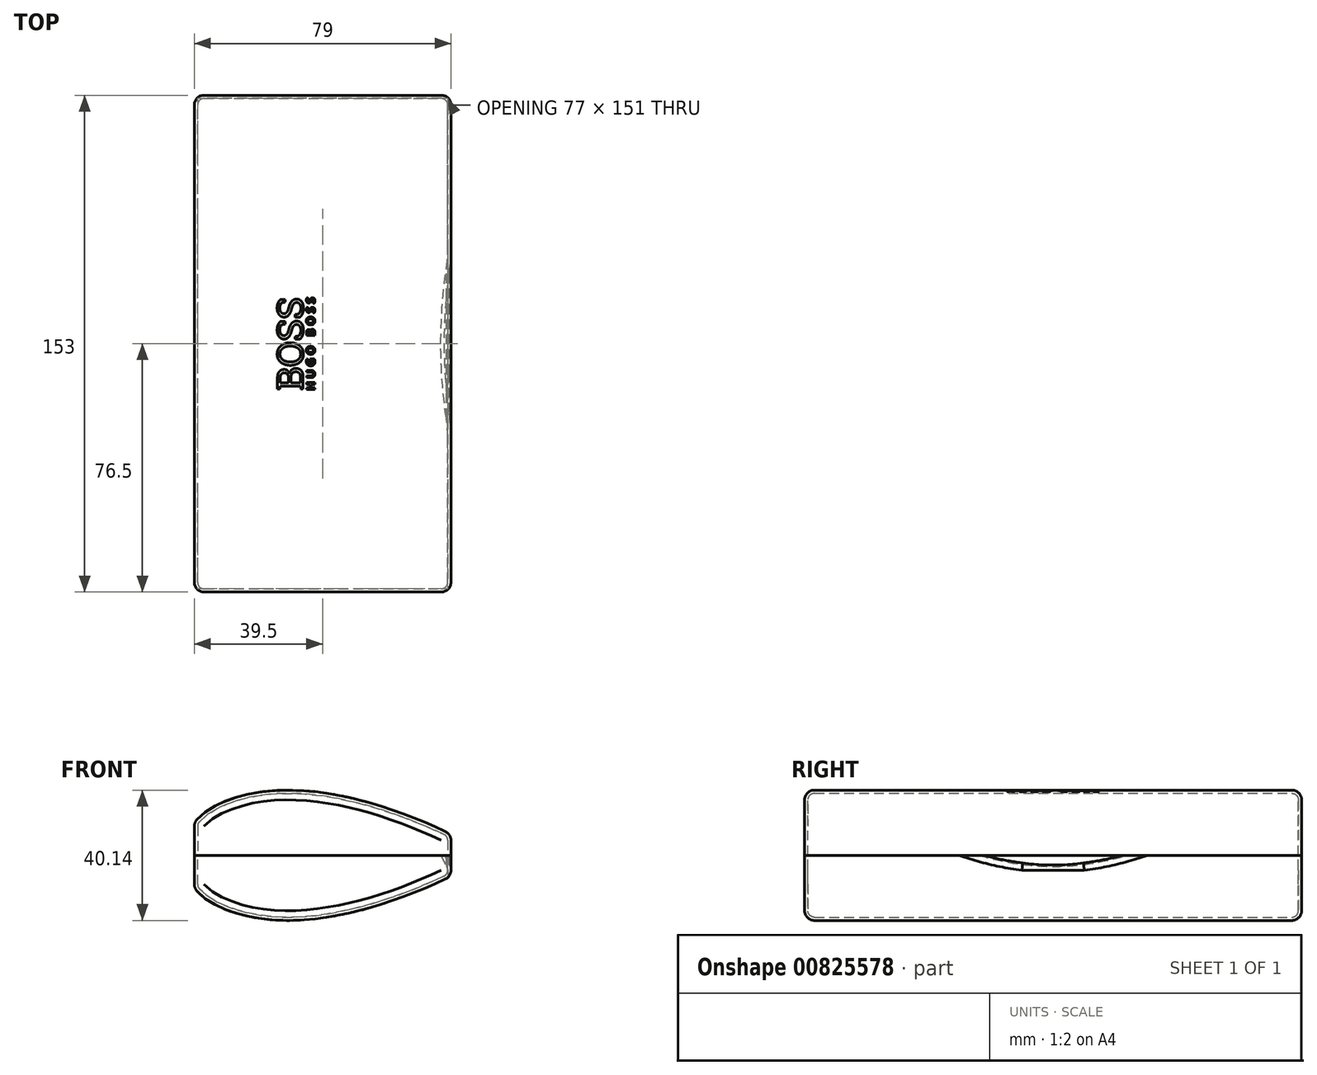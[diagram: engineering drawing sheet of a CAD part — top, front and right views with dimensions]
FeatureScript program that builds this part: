
annotation { "Feature Type Name" : "Feature", "Feature Type Description" : "" }
export const myFeature = defineFeature(function(context is Context, id is Id, definition is map)
    precondition{}
    {
        {
            var Q0;
            Q0=qCreatedBy(makeId("Front.planeOp"),FACE);
            var sketch = newSketch(context, id + "F0", { "sketchPlane" : qUnion([Q0])});
            skLineSegment(sketch, "E0", {"start": v(-39.5, 0) * mm, "end": v(39.5, 0) * mm});
            skLineSegment(sketch, "E1", {"start": v(39.5, 6.5) * mm, "end": v(39.5, -6.5) * mm});
            skLineSegment(sketch, "E2", {"start": v(-39.5, 10) * mm, "end": v(-39.5, -10) * mm});
            skPoint(sketch, "E3", {"position": v(-14.5, 20) * mm});
            skPoint(sketch, "E4", {"position": v(-39.5, 0) * mm});
            skFitSpline(sketch, "E5", {"points": [v(-39.5, 10) * mm, v(-13.74, 20) * mm, v(39.5, 6.5) * mm], "startDerivative": vector(26.63, 38.18) * mm, "endDerivative": vector(85.64, -41.52) * mm});
            skSolve(sketch);
        }
        {
            var Q0;
            {var subQ0=sQuery(id+"F0.wireOp",EDGE,"E0");Q0=makeQuery(id+"F0.imprint","IMPRINT",FACE,{"disambiguationData":[TD([[makeQuery(id+"F0.imprint","IMPRINT",EDGE,{"derivedFrom":subQ0}),1.0]])]});}
            extrude(context, id + "F1", {"entities" : qUnion([Q0]), "endBound" : BoundingType.SYMMETRIC, "depth" : 153 * mm, "offsetDistance" : 25 * mm});
        }
        {
            var Q0;
            Q0=makeQuery(id+"F1.opExtrude","SWEPT_BODY",BODY,{"disambiguationData":[OSD([sQuery(id+"F0.wireOp",EDGE,"E0"),sQuery(id+"F0.wireOp",EDGE,"E1"),sQuery(id+"F0.wireOp",EDGE,"E2"),sQuery(id+"F0.wireOp",EDGE,"E5")])]});
            var Q1;
            Q1=makeQuery(id+"F1.opExtrude","SWEPT_FACE",FACE,{"disambiguationData":[OSD([sQuery(id+"F0.wireOp",EDGE,"E0")])]});
            mirror(context, id + "F2", {"entities" : qUnion([Q0]), "mirrorPlane" : qUnion([Q1])});
        }
        {
            var Q0;
            Q0=makeQuery(id+"F2.opPattern","COPY",FACE,{"derivedFrom":makeQuery(id+"F1.opExtrude","SWEPT_FACE",FACE,{"disambiguationData":[OSD([sQuery(id+"F0.wireOp",EDGE,"E0")])]}),"instanceName":"1"});
            var sketch = newSketch(context, id + "F3", { "sketchPlane" : qUnion([Q0])});
            skLineSegment(sketch, "E6", {"start": v(0, 0) * mm, "end": v(39.5, 0) * mm, "construction": true});
            skLineSegment(sketch, "E7", {"start": v(39.5, 25) * mm, "end": v(39.5, -25) * mm});
            skLineSegment(sketch, "E8", {"start": v(39.5, 0) * mm, "end": v(37.5, 0) * mm, "construction": true});
            skArc(sketch, "E9", {"start": v(39.5, 25) * mm, "mid": v(37.5, 0) * mm, "end": v(39.5, -25) * mm});
            skSolve(sketch);
        }
        {
            var Q0;
            Q0=qCreatedBy(makeId("Front.planeOp"),FACE);
            var sketch = newSketch(context, id + "F4", { "sketchPlane" : qUnion([Q0])});
            skPoint(sketch, "E10", {"position": v(37.5, 0) * mm});
            skPoint(sketch, "E11", {"position": v(39.5, -4) * mm});
            skLineSegment(sketch, "E12", {"start": v(37.5, 0) * mm, "end": v(39.5, -4) * mm});
            skSolve(sketch);
        }
        {
            var Q0;
            Q0=makeQuery(id+"F3.imprint","IMPRINT",FACE,{"disambiguationData":[TD([[makeQuery(id+"F3.imprint","IMPRINT",EDGE,{"derivedFrom":sQuery(id+"F3.wireOp",EDGE,"E7")}),1.0]])]});
            var Q1;
            Q1=sQuery(id+"F4.wireOp",EDGE,"E12");
            sweep(context, id + "F5", {"operationType" : NewBodyOperationType.REMOVE, "profiles" : qUnion([Q0]), "path" : qUnion([Q1])});
        }
        {
            var Q0;
            Q0=makeQuery(id+"F1.opExtrude","SWEPT_FACE",FACE,{"disambiguationData":[OSD([sQuery(id+"F0.wireOp",EDGE,"E5")])]});
            var Q1;
            Q1=makeQuery(id+"F2.opPattern","COPY",FACE,{"derivedFrom":makeQuery(id+"F1.opExtrude","SWEPT_FACE",FACE,{"disambiguationData":[OSD([sQuery(id+"F0.wireOp",EDGE,"E5")])]}),"instanceName":"1"});
            var Q2;
            Q2=makeQuery(id+"F1.opExtrude","CAP_EDGE",EDGE,{"disambiguationData":[OSD([sQuery(id+"F0.wireOp",EDGE,"E1")])],"isStart":false});
            var Q3;
            Q3=makeQuery(id+"F2.opPattern","COPY",EDGE,{"derivedFrom":makeQuery(id+"F1.opExtrude","CAP_EDGE",EDGE,{"disambiguationData":[OSD([sQuery(id+"F0.wireOp",EDGE,"E1")])],"isStart":false}),"instanceName":"1"});
            var Q4;
            Q4=makeQuery(id+"F1.opExtrude","CAP_EDGE",EDGE,{"disambiguationData":[OSD([sQuery(id+"F0.wireOp",EDGE,"E1")])],"isStart":true});
            var Q5;
            Q5=makeQuery(id+"F2.opPattern","COPY",EDGE,{"derivedFrom":makeQuery(id+"F1.opExtrude","CAP_EDGE",EDGE,{"disambiguationData":[OSD([sQuery(id+"F0.wireOp",EDGE,"E1")])],"isStart":true}),"instanceName":"1"});
            var Q6;
            Q6=makeQuery(id+"F1.opExtrude","CAP_EDGE",EDGE,{"disambiguationData":[OSD([sQuery(id+"F0.wireOp",EDGE,"E2")])],"isStart":true});
            var Q7;
            Q7=makeQuery(id+"F2.opPattern","COPY",EDGE,{"derivedFrom":makeQuery(id+"F1.opExtrude","CAP_EDGE",EDGE,{"disambiguationData":[OSD([sQuery(id+"F0.wireOp",EDGE,"E2")])],"isStart":true}),"instanceName":"1"});
            var Q8;
            Q8=makeQuery(id+"F1.opExtrude","CAP_EDGE",EDGE,{"disambiguationData":[OSD([sQuery(id+"F0.wireOp",EDGE,"E2")])],"isStart":false});
            var Q9;
            Q9=makeQuery(id+"F2.opPattern","COPY",EDGE,{"derivedFrom":makeQuery(id+"F1.opExtrude","CAP_EDGE",EDGE,{"disambiguationData":[OSD([sQuery(id+"F0.wireOp",EDGE,"E2")])],"isStart":false}),"instanceName":"1"});
            fillet(context, id + "F6", {"entities" : qUnion([Q0, Q1, Q2, Q3, Q4, Q5, Q6, Q7, Q8, Q9]), "radius" : 3 * mm, "tangentPropagation" : true, "allowEdgeOverflow" : false});
        }
        {
            var Q0;
            Q0=makeQuery(id+"F5.boolean.opBoolean","INTERSECT",EDGE,{"derivedFrom":[makeQuery(id+"F2.opPattern","COPY",FACE,{"derivedFrom":makeQuery(id+"F1.opExtrude","SWEPT_FACE",FACE,{"disambiguationData":[OSD([sQuery(id+"F0.wireOp",EDGE,"E1")])]}),"instanceName":"1"}),makeQuery(id+"F5.opSweep","SWEPT_FACE",FACE,{"disambiguationData":[OSD([sQuery(id+"F3.wireOp",EDGE,"E9"),sQuery(id+"F4.wireOp",EDGE,"E12")])]})]});
            fillet(context, id + "F7", {"entities" : qUnion([Q0]), "radius" : 5 * mm, "tangentPropagation" : true, "allowEdgeOverflow" : false});
        }
        {
            var Q0;
            Q0=makeQuery(id+"F2.opPattern","COPY",FACE,{"derivedFrom":makeQuery(id+"F1.opExtrude","SWEPT_FACE",FACE,{"disambiguationData":[OSD([sQuery(id+"F0.wireOp",EDGE,"E0")])]}),"instanceName":"1"});
            var Q1;
            Q1=makeQuery(id+"F1.opExtrude","SWEPT_FACE",FACE,{"disambiguationData":[OSD([sQuery(id+"F0.wireOp",EDGE,"E0")])]});
            shell(context, id + "F8", {"entities" : qUnion([Q0, Q1]), "thickness" : 1 * mm});
        }
        {
            var Q0;
            Q0=qCreatedBy(makeId("Top.planeOp"),FACE);
            cPlane(context, id + "F9", {"entities" : qUnion([Q0]), "cplaneType" : CPlaneType.OFFSET, "offset" : 50 * mm, "width" : 150 * mm, "height" : 150 * mm});
        }
        {
            var Q0;
            Q0=qCreatedBy(id+"F9.planeOp",FACE);
            var sketch = newSketch(context, id + "F10", { "sketchPlane" : qUnion([Q0])});
            skLineSegment(sketch, "E13.0.0", {"start": v(37.78, -73.5) * mm, "end": v(37.78, 73.5) * mm});
            skFitSpline(sketch, "E13.0.1", {"points": [v(37.78, 73.5) * mm, v(12.26, 73.5) * mm, v(-13.25, 73.5) * mm, v(-38.77, 73.5) * mm]});
            skLineSegment(sketch, "E13.0.2", {"start": v(-38.77, 73.5) * mm, "end": v(-38.77, -73.5) * mm});
            skFitSpline(sketch, "E13.0.3", {"points": [v(-38.77, -73.5) * mm, v(-13.25, -73.5) * mm, v(12.26, -73.5) * mm, v(37.78, -73.5) * mm]});
            skLineSegment(sketch, "E14", {"start": v(-38.77, -73.5) * mm, "end": v(37.78, 73.5) * mm, "construction": true});
            skLineSegment(sketch, "E15", {"start": v(-38.77, 73.5) * mm, "end": v(37.78, -73.5) * mm, "construction": true});
            skPoint(sketch, "E16", {"position": v(-0.5, 0) * mm});
            skText(sketch, "E17", { "text": "BOSS", "fontName": "RobotoSlab-Regular.ttf"});
            skText(sketch, "E18", { "text": "H U G O   B O S S", "fontName": "OpenSans-Bold.ttf"});
            const initialGuessF10  = {"E17": [-0.00602, -0.01442, 0, 1, 0.008], "E18": [-0.00242, -0.01442, 0, 1, 0.0026]};
            skSetInitialGuess(sketch, initialGuessF10);
            skSolve(sketch);
        }
        {
            var Q0;
            Q0=makeQuery(id+"F10.imprint","IMPRINT",FACE,{"disambiguationData":[TD([[makeQuery(id+"F10.imprint","IMPRINT",EDGE,{"derivedFrom":sQuery(id+"F10.wireOp",EDGE,"E17.sketch_text.stroke-0")}),-1.0]])]});
            var Q1;
            Q1=makeQuery(id+"F10.imprint","IMPRINT",FACE,{"disambiguationData":[TD([[makeQuery(id+"F10.imprint","IMPRINT",EDGE,{"derivedFrom":sQuery(id+"F10.wireOp",EDGE,"E17.sketch_text.stroke-30")}),-1.0]])]});
            var Q2;
            Q2=makeQuery(id+"F10.imprint","IMPRINT",FACE,{"disambiguationData":[TD([[makeQuery(id+"F10.imprint","IMPRINT",EDGE,{"derivedFrom":sQuery(id+"F10.wireOp",EDGE,"E17.sketch_text.stroke-50")}),-1.0]])]});
            var Q3;
            Q3=makeQuery(id+"F10.imprint","IMPRINT",FACE,{"disambiguationData":[TD([[makeQuery(id+"F10.imprint","IMPRINT",EDGE,{"derivedFrom":sQuery(id+"F10.wireOp",EDGE,"E17.sketch_text.stroke-80")}),-1.0]])]});
            var Q4;
            Q4=makeQuery(id+"F10.imprint","IMPRINT",FACE,{"disambiguationData":[TD([[makeQuery(id+"F10.imprint","IMPRINT",EDGE,{"derivedFrom":sQuery(id+"F10.wireOp",EDGE,"E18.sketch_text.stroke-127")}),-1.0]])]});
            var Q5;
            Q5=makeQuery(id+"F10.imprint","IMPRINT",FACE,{"disambiguationData":[TD([[makeQuery(id+"F10.imprint","IMPRINT",EDGE,{"derivedFrom":sQuery(id+"F10.wireOp",EDGE,"E18.sketch_text.stroke-99")}),-1.0]])]});
            var Q6;
            Q6=makeQuery(id+"F10.imprint","IMPRINT",FACE,{"disambiguationData":[TD([[makeQuery(id+"F10.imprint","IMPRINT",EDGE,{"derivedFrom":sQuery(id+"F10.wireOp",EDGE,"E18.sketch_text.stroke-85")}),-1.0]])]});
            var Q7;
            Q7=makeQuery(id+"F10.imprint","IMPRINT",FACE,{"disambiguationData":[TD([[makeQuery(id+"F10.imprint","IMPRINT",EDGE,{"derivedFrom":sQuery(id+"F10.wireOp",EDGE,"E18.sketch_text.stroke-60")}),-1.0]])]});
            var Q8;
            Q8=makeQuery(id+"F10.imprint","IMPRINT",FACE,{"disambiguationData":[TD([[makeQuery(id+"F10.imprint","IMPRINT",EDGE,{"derivedFrom":sQuery(id+"F10.wireOp",EDGE,"E18.sketch_text.stroke-12")}),-1.0]])]});
            var Q9;
            Q9=makeQuery(id+"F10.imprint","IMPRINT",FACE,{"disambiguationData":[TD([[makeQuery(id+"F10.imprint","IMPRINT",EDGE,{"derivedFrom":sQuery(id+"F10.wireOp",EDGE,"E18.sketch_text.stroke-27")}),-1.0]])]});
            var Q10;
            Q10=makeQuery(id+"F10.imprint","IMPRINT",FACE,{"disambiguationData":[TD([[makeQuery(id+"F10.imprint","IMPRINT",EDGE,{"derivedFrom":sQuery(id+"F10.wireOp",EDGE,"E18.sketch_text.stroke-46")}),-1.0]])]});
            var Q11;
            Q11=makeQuery(id+"F10.imprint","IMPRINT",FACE,{"disambiguationData":[TD([[makeQuery(id+"F10.imprint","IMPRINT",EDGE,{"derivedFrom":sQuery(id+"F10.wireOp",EDGE,"E18.sketch_text.stroke-0")}),-1.0]])]});
            extrude(context, id + "F11", {"entities" : qUnion([Q0, Q1, Q2, Q3, Q4, Q5, Q6, Q7, Q8, Q9, Q10, Q11]), "operationType" : NewBodyOperationType.REMOVE, "endBound" : BoundingType.UP_TO_NEXT, "oppositeDirection" : true, "depth" : 25 * mm, "hasOffset" : true, "offsetDistance" : -.2 * mm});
        }
    });
